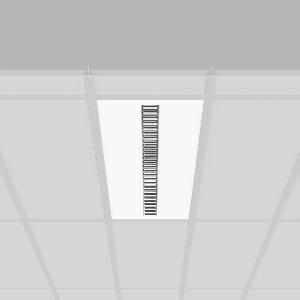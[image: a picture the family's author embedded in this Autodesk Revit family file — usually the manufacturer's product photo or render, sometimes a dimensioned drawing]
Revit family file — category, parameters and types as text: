
# Revit family: sonis_901681_002_1_76_7d14
name_source: partatom
category: Lighting Fixtures
units: mm (PartAtom-declared; Revit-internal decimal feet)

## family parameters
Cut with Voids When Loaded = No
Host = Face
Light Source = No
Part Type = Normal
Room Calculation Point = No
Round Connector Dimension = Use Diameter
Shared = No

## types (1)
- Sonis (1 x LED Modul 840, 3450 lm, 4000)
    Apparent Load = 26 VA
    CIE Flux Codes = 83 100 100 100 100
    Color Rendering = 80
    Color Temperature = 4000
    Default Elevation = 1800 mm
    Description = Series: SONIS
High-efficiency lay-in luminaire for ceiling systems with visible mounting rails. Housing: metal, powder-coated. Alea optical system: Reflector structure (ABS, Aluminium-coated, highly polished) with integrated diffuser made of non-yellowing plastic (PMMA) opal for glare-free light at the workstation. Narrow beam, brilliant luminous effect. Suitable for Recessed ceiling mounting. Driver integrated. Perfect for office areas (RUG < 19) and environments with computer screens in accordance with EN 12464-1. 
Colour: white
Length: 1247 mm
Width: 310 mm
Cut-out length: 1225 mm
Cut-out width: 285 mm
Recess height: 27 mm
Lamp: LED
Socket: without socket
Colour temperature: 4000K
Colour rendering index (CRI): 80
System power: 26 W
Rated luminous flux: 3450 lm
Luminous efficiency: 133 lm/W
Control gear: Converter, dimmable, DALI
Protection class: I
Type of protection: IP 20
    Height = 0 mm  [stored 0 ft]
    Lamp = 1 x LED Modul 840
    Lamp Light Flux = 3450 lm
    Lamp count = 1
    Length = 1247 mm
    Lifetime = 50000 h
    Luminous efficacy = 133 lm/W
    Manufacturer = RZB
    ModVariant = No
    Model = 901681.002.1.76
    Mounting Place = Ceiling
    Mounting Type = Recessed
    Number of Poles = 1
    OnlyDefault = Yes
    Power Factor = 1
    Product Name = Sonis
    Product group = Recessed modular luminaires
    ProductGroupID = 406
    Protection Class = Protection class I
    Protection Degree = IP 20
    RLX_Detail_Level = 1
    RLX_Emergency_Light_Flux = 0 lm
    RLX_Emergency_Type = 0
    RLX_Emergency_Type_DB = No
    RlxData = <blob elided: 33401 chars, md5=61ac5835>
    Socket = socket
    Standby Power = 0 W
    System Light Flux = 3450 lm
    System Power = 26 W
    Type Comments = Product without accessories
    Type Image = 901623.002.jpg
    URL = http://relux.com
    VarID = ---
    Voltage = 0 V
    Weight = 0.00 kg
    Width = 310 mm

note: [stored X ft] marks values corroborated as IEEE doubles in the binary element streams (Revit-internal decimal feet)

## geometry (parser evidence)
native form markers: Blend x4, Sweep x8
no freeform markers — native parametric forms only
